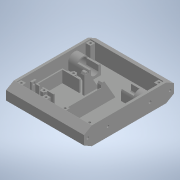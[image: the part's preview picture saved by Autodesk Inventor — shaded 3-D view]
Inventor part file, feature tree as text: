
AUTODESK INVENTOR PART (.ipt)
format: ipt  version: 2020 (Build 240168000, 168)  size: 606,720 bytes
history: native  units: in
note: dims shown in document units (in); Inventor stores cm internally (conversion verified against a paired STEP export)
features: extrude x18, sketch x17, projected_geometry x14, mirror x6, plane x1
ambient origin geometry x8: Origin, YZ Plane, XZ Plane, XY Plane, X Axis, Y Axis, Z Axis, Center Point
bodies: Solid1 (feature_tree)
feature tree (56):
  extrude  "Extrusion1"  Depth=5.9055in
  extrude  "Extrusion2"  TaperAngle=0.0deg  [1 undecoded]
  extrude  "Extrusion3"  Depth=1.063in
  extrude  "Extrusion4"  Depth=0.315in
  extrude  "Extrusion5"  TaperAngle=0.0deg  [1 undecoded]
  extrude  "Extrusion6"  Depth=0.5906in
  mirror  "Mirror1"
  extrude  "Extrusion7"  Depth=0.0787in
  mirror  "Mirror2"
  extrude  "Extrusion8"  Depth=0.6102in
  mirror  "Mirror3"
  plane  "Work Plane1"
  extrude  "Extrusion9"  Depth=0.7874in TaperAngle=0.0deg
  mirror  "Mirror4"
  extrude  "Extrusion10"  Depth=0.1654in TaperAngle=0.0deg
  extrude  "Extrusion11"  Depth=0.1575in
  extrude  "Extrusion12"  TaperAngle=0.0deg  [1 undecoded]
  extrude  "Extrusion13"  Depth=0.2756in
  extrude  "Extrusion14"  Depth=0.4331in
  extrude  "Extrusion17"  Depth=2.7559in
  extrude  "Extrusion18"  Depth=0.0413in
  mirror  "Mirror6"
  extrude  "Extrusion19"  TaperAngle=0.0deg  [1 undecoded]
  mirror  "Mirror7"
  extrude  "Extrusion20"  TaperAngle=60.0deg  [1 undecoded]
  sketch  "Sketch1"  dims[d0=1.1811in d1=5.9055in]
  sketch  "Sketch2"  dims[d2=5.1181in d3=0.0in]
  projected_geometry  "Projected Loop1"
  sketch  "Sketch3"  dims[d4=0.1575in d5=1.063in]
  projected_geometry  "Projected Loop2"
  projected_geometry  "Projected Loop3"
  sketch  "Sketch4"  dims[d6=0.0in d8=0.315in]
  projected_geometry  "Projected Loop4"
  sketch  "Sketch6"  dims[d10=0.993in d11=0.0in]
  sketch  "Sketch7"  dims[d12=0.6496in d13=0.5906in]
  sketch  "Sketch9"  dims[d14=1.5748in d15=0.0787in]
  sketch  "Sketch10"  dims[d16=0.5512in d17=0.0in d18=0.6102in]
  sketch  "Sketch12"  dims[d19=0.4803in d20=0.7874in d21=0.0in]
  projected_geometry  "Projected Loop6"
  projected_geometry  "Projected Loop7"
  projected_geometry  "Projected Loop8"
  sketch  "Sketch13"  dims[d22=0.1654in d23=6.063in d24=0.0in]
  sketch  "Sketch14"  dims[d25=0.5114in d26=0.1575in]
  sketch  "Sketch15"  dims[d27=1.5748in d28=0.0in d29=0.0in]
  projected_geometry  "Projected Loop15"
  sketch  "Sketch16"  dims[d30=0.1575in d31=0.2756in]
  projected_geometry  "Projected Loop19"
  projected_geometry  "Projected Loop20"
  projected_geometry  "Projected Loop21"
  projected_geometry  "Projected Loop22"
  projected_geometry  "Projected Loop23"
  projected_geometry  "Projected Loop24"
  sketch  "Sketch20"  dims[d32=0.0in d33=0.4331in]
  sketch  "Sketch21"  dims[d34=0.0827in d38=2.7559in]
  sketch  "Sketch22"  dims[d40=0.0413in d41=0.0909in]
  sketch  "Sketch23"  dims[d42=0.2362in d43=0.0in d44=60.0deg d45=0.0787in d46=0.315in d48=0.993in d49=0.0in d53=0.2756in d54=0.0in d55=0.4724in d56=1.2008in d57=1.6142in d58=1.5945in d59=0.0787in d60=0.0787in d62=0.315in d63=0.7677in d64=0.0in d66=0.1476in d67=0.2756in d68=0.0in d69=0.7874in d70=0.2953in d71=0.1181in d72=0.0in d89=0.0157in d90=0.0157in d91=0.1476in d92=0.1476in d96=0.315in d97=0.1575in d98=0.1181in d99=0.0in d102=0.1772in d104=0.3346in d105=135.0deg d106=0.2362in d107=0.0in d108=0.0394in d109=0.0in d110=0.0315in d111=0.0394in d112=0.0in]
note: 5 required parameter values undecoded (feature->parameter linkage not recoverable at this tier; creation-order binding heuristic only, values carry confidence <= 0.55)
